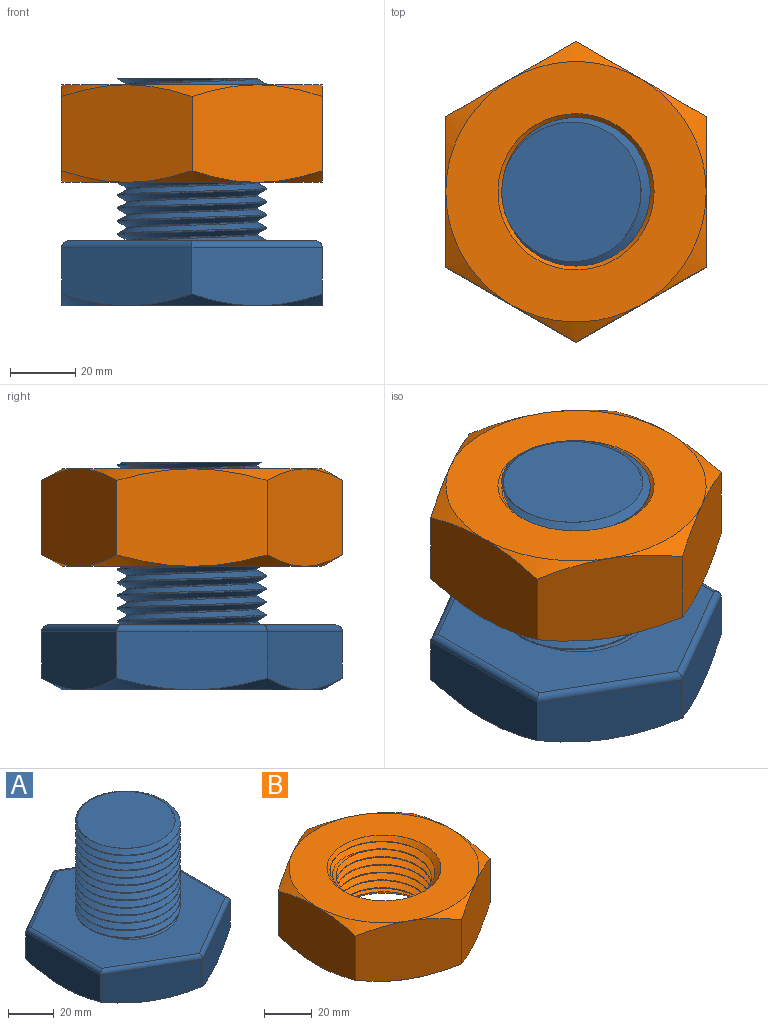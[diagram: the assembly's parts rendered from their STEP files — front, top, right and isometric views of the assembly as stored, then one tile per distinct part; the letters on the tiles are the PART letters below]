
ASSEMBLY  parts=2 mates=1
PART A: 26 faces, bbox 94.2x94.2x73.7 mm
  f0: plane 89.63x77.87mm, normal (0,0,1), area 3560.6mm2, adj f1,f3,f4,f18,f19,f20,f21,f22
  f1: cylinder r=20mm len=50mm, axis (0,0,-1), area 589.8mm2, adj f0,f2,f4,f24,f25
  f2: bspline ~52.65x51.62mm, area 5334.1mm2, adj f1,f3,f24,f25
  f3: cylinder r=22.8mm len=50mm, axis (0,0,1), area 1085.3mm2, adj f0,f2,f4,f24,f25
  f4: bspline ~53.62x52.65mm, area 5438.3mm2, adj f0,f1,f3,f24
  f5: plane 46.2x18mm, normal (-1,0,0), area 774.8mm2, adj f6,f10,f12,f16,f19
  f6: plane 40x23.09mm, normal (-0.5,-0.87,0), area 774.8mm2, adj f5,f7,f15,f16,f18
  f7: plane 40x23.09mm, normal (0.5,-0.87,0), area 774.8mm2, adj f6,f8,f14,f15,f20
  f8: plane 46.2x18mm, normal (1,0,0), area 774.8mm2, adj f7,f9,f13,f14,f22
  f9: plane 40x23.09mm, normal (0.5,0.87,0), area 774.8mm2, adj f8,f10,f11,f13,f23
  f10: plane 40x23.09mm, normal (-0.5,0.87,0), area 774.8mm2, adj f5,f9,f11,f12,f21
  f11: cone r=50mm half-angle=60deg, axis (0,0,1), area 99.3mm2, adj f9,f10,f17
  f12: cone r=50mm half-angle=60deg, axis (0,0,1), area 99.3mm2, adj f5,f10,f17
  f13: cone r=50mm half-angle=60deg, axis (0,0,1), area 99.3mm2, adj f8,f9,f17
  f14: cone r=50mm half-angle=60deg, axis (0,0,1), area 99.3mm2, adj f7,f8,f17
  f15: cone r=50mm half-angle=60deg, axis (0,0,1), area 99.3mm2, adj f6,f7,f17
  f16: cone r=50mm half-angle=60deg, axis (0,0,1), area 99.3mm2, adj f5,f6,f17
  f17: plane 80x80mm, normal (0,0,-1), area 5026.5mm2, adj f11,f12,f13,f14,f15,f16
  f18: cylinder r=2mm len=41mm, axis (-0.87,0.5,0), area 141.5mm2, adj f0,f6,f19,f20
  f19: cylinder r=2mm len=46.19mm, axis (0,1,0), area 141.5mm2, adj f0,f5,f18,f21
  f20: cylinder r=2mm len=41mm, axis (-0.87,-0.5,0), area 141.5mm2, adj f0,f7,f18,f22
  f21: cylinder r=2mm len=41mm, axis (0.87,0.5,0), area 141.5mm2, adj f0,f10,f19,f23
  f22: cylinder r=2mm len=46.19mm, axis (0,-1,0), area 141.5mm2, adj f0,f8,f20,f23
  f23: cylinder r=2mm len=41mm, axis (0.87,-0.5,0), area 141.5mm2, adj f0,f9,f21,f22
  f24: plane 44.74x44.67mm, normal (0,0,1), area 1441.5mm2, adj f1,f2,f3,f4
  f25: bspline ~45.6x26.33mm, area 106.8mm2, adj f0,f1,f2,f3
PART B: 27 faces, bbox 92.4x92.4x31.6 mm
  f0: plane 40x30.01mm, normal (-0.5,0.87,0), area 1272.4mm2, adj f1,f5,f6,f7,f8,f9
  f1: plane 40x30.01mm, normal (0.5,0.87,0), area 1272.4mm2, adj f0,f2,f6,f8,f10,f11
  f2: plane 46.2x30.01mm, normal (1,0,0), area 1272.4mm2, adj f1,f3,f10,f11,f12,f13
  f3: plane 40x30.01mm, normal (0.5,-0.87,0), area 1272.4mm2, adj f2,f4,f12,f13,f14,f15
  f4: plane 40x30.01mm, normal (-0.5,-0.87,0), area 1272.4mm2, adj f3,f5,f14,f15,f16,f17
  f5: plane 46.2x30.01mm, normal (-1,0,0), area 1272.4mm2, adj f0,f4,f7,f9,f16,f17
  f6: cone r=65mm half-angle=60deg, axis (0,0,1), area 99.3mm2, adj f0,f1,f18
  f7: cone r=65mm half-angle=60deg, axis (0,0,1), area 99.3mm2, adj f0,f5,f18
  f8: cone r=65mm half-angle=60deg, axis (0,0,-1), area 99.3mm2, adj f0,f1,f19
  f9: cone r=65mm half-angle=60deg, axis (0,0,-1), area 99.3mm2, adj f0,f5,f19
  f10: cone r=65mm half-angle=60deg, axis (0,0,1), area 99.3mm2, adj f1,f2,f18
  f11: cone r=65mm half-angle=60deg, axis (0,0,-1), area 99.3mm2, adj f1,f2,f19
  f12: cone r=65mm half-angle=60deg, axis (0,0,1), area 99.3mm2, adj f2,f3,f18
  f13: cone r=65mm half-angle=60deg, axis (0,0,-1), area 99.3mm2, adj f2,f3,f19
  f14: cone r=65mm half-angle=60deg, axis (0,0,1), area 99.3mm2, adj f3,f4,f18
  f15: cone r=65mm half-angle=60deg, axis (0,0,-1), area 99.3mm2, adj f3,f4,f19
  f16: cone r=65mm half-angle=60deg, axis (0,0,1), area 99.3mm2, adj f4,f5,f18
  f17: cone r=65mm half-angle=60deg, axis (0,0,-1), area 99.3mm2, adj f4,f5,f19
  f18: plane 80x80mm, normal (0,0,-1), area 3217mm2, adj f6,f7,f10,f12,f14,f16,f23
  f19: plane 80x80mm, normal (0,0,1), area 3217mm2, adj f8,f9,f11,f13,f15,f17,f21
  f20: cylinder r=20mm len=40mm, axis (0,0,-1), area 259.2mm2, adj f21,f22,f24,f26
  f21: cone r=24mm half-angle=45deg, axis (0,0,1), area 519.9mm2, adj f19,f20,f24,f25,f26
  f22: cone r=20mm half-angle=45deg, axis (0,0,-1), area 67.5mm2, adj f20,f23,f24,f26
  f23: cone r=20mm half-angle=45deg, axis (0,0,-1), area 452.7mm2, adj f18,f22,f25,f26
  f24: bspline ~52.65x45.6mm, area 2706.4mm2, adj f20,f21,f22,f25
  f25: cylinder r=22.8mm len=45.6mm, axis (0,0,1), area 562.5mm2, adj f21,f23,f24,f26
  f26: bspline ~52.65x45.6mm, area 2705.5mm2, adj f20,f21,f22,f23,f25
PLACE A t=(-50.27,59.74,61.29)mm
PLACE B t=(149.73,59.74,99.25)mm fixed
MATE parallel B.f6 <-> A.f0  axis (0,0,-1) through (149.73,59.74,99.25)mm
